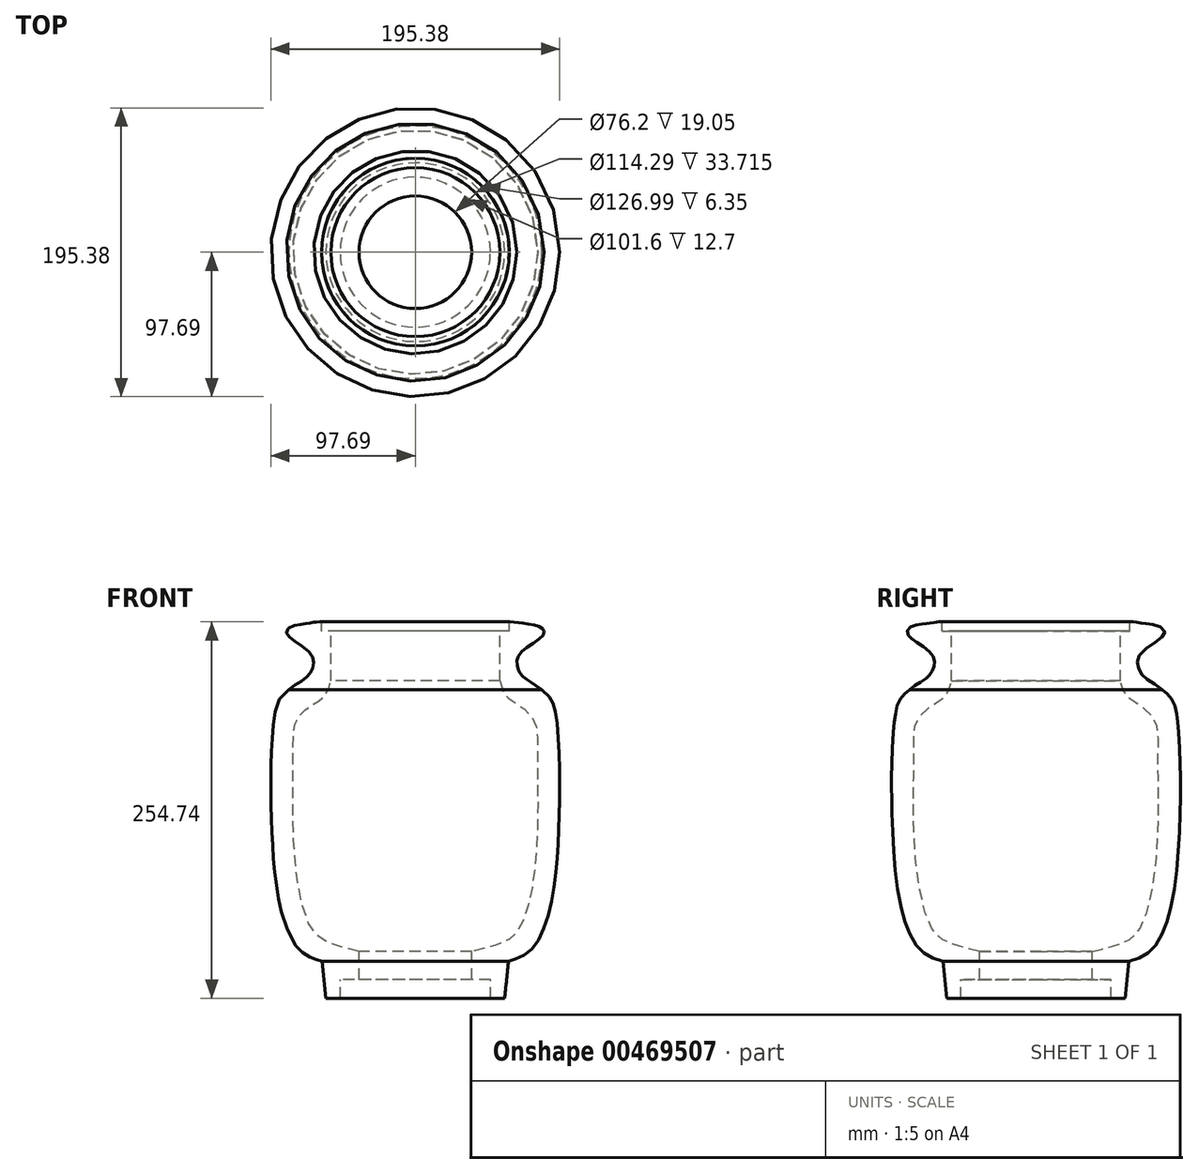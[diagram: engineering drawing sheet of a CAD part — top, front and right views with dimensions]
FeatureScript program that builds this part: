
annotation { "Feature Type Name" : "Feature", "Feature Type Description" : "" }
export const myFeature = defineFeature(function(context is Context, id is Id, definition is map)
    precondition{}
    {
        {
            var Q0;
            Q0=qCreatedBy(makeId("Front.planeOp"),FACE);
            var sketch = newSketch(context, id + "F0", { "sketchPlane" : qUnion([Q0])});
            skLineSegment(sketch, "E0", {"start": v(-38.1, 12.7) * mm, "end": v(-50.8, 12.7) * mm});
            skLineSegment(sketch, "E1", {"start": v(-50.8, 12.7) * mm, "end": v(-50.8, 0) * mm});
            skLineSegment(sketch, "E2", {"start": v(-50.8, 0) * mm, "end": v(-60.45, 0) * mm});
            skLineSegment(sketch, "E3", {"start": v(-60.45, 0) * mm, "end": v(-63, 24.85) * mm});
            skFitSpline(sketch, "E4", {"points": [v(-85.47, 208.82) * mm, v(-94.45, 195.79) * mm, v(-97.62, 152.8) * mm, v(-96.67, 106.19) * mm, v(-91.44, 62.48) * mm, v(-77.33, 31.7) * mm, v(-63, 24.85) * mm], "startDerivative": vector(-152.35, -127.25) * mm, "endDerivative": vector(97.69, -34.04) * mm});
            skLineSegment(sketch, "E5", {"start": v(-38.1, 12.7) * mm, "end": v(-38.1, 31.75) * mm});
            skFitSpline(sketch, "E6", {"points": [v(-57.15, 214.67) * mm, v(-64.64, 201.7) * mm, v(-79.3, 190.05) * mm, v(-82.65, 164.15) * mm, v(-81.94, 100.01) * mm, v(-69.15, 45.34) * mm, v(-57.73, 37.19) * mm, v(-38.1, 31.75) * mm], "startDerivative": vector(-58.43, -235.9) * mm, "endDerivative": vector(313.05, -69.63) * mm});
            skLineSegment(sketch, "E7", {"start": v(0, 215.33) * mm, "end": v(0, 0) * mm, "construction": true});
            skPoint(sketch, "E8", {"position": v(-82.65, 152.8) * mm});
            skFitSpline(sketch, "E9", {"points": [v(-85.47, 208.82) * mm, v(-73.2, 217.43) * mm, v(-69.08, 224.57) * mm, v(-71.13, 233.58) * mm, v(-86.7, 246.3) * mm, v(-85.47, 250.8) * mm, v(-73.18, 253.67) * mm, v(-63.5, 254.74) * mm], "startDerivative": vector(97.94, 76.94) * mm, "endDerivative": vector(80.77, -1.22) * mm});
            skLineSegment(sketch, "E10", {"start": v(-63.5, 254.74) * mm, "end": v(-63.5, 248.39) * mm});
            skLineSegment(sketch, "E11", {"start": v(-63.5, 248.39) * mm, "end": v(-57.15, 248.39) * mm});
            skLineSegment(sketch, "E12", {"start": v(-57.15, 248.39) * mm, "end": v(-57.15, 214.67) * mm});
            skLineSegment(sketch, "E13", {"start": v(0, 215.33) * mm, "end": v(0, -75.14) * mm});
            skSolve(sketch);
        }
        {
            var Q0;
            Q0=makeQuery(id+"F0.imprint","IMPRINT",FACE,{"disambiguationData":[TD([[makeQuery(id+"F0.imprint","IMPRINT",EDGE,{"derivedFrom":sQuery(id+"F0.wireOp",EDGE,"E0")}),-1.0]])]});
            var Q1;
            Q1=sQuery(id+"F0.wireOp",EDGE,"E7");
            revolve(context, id + "F1", {"entities" : qUnion([Q0]), "axis" : qUnion([Q1]), "revolveType" : RevolveType.FULL});
        }
    });
